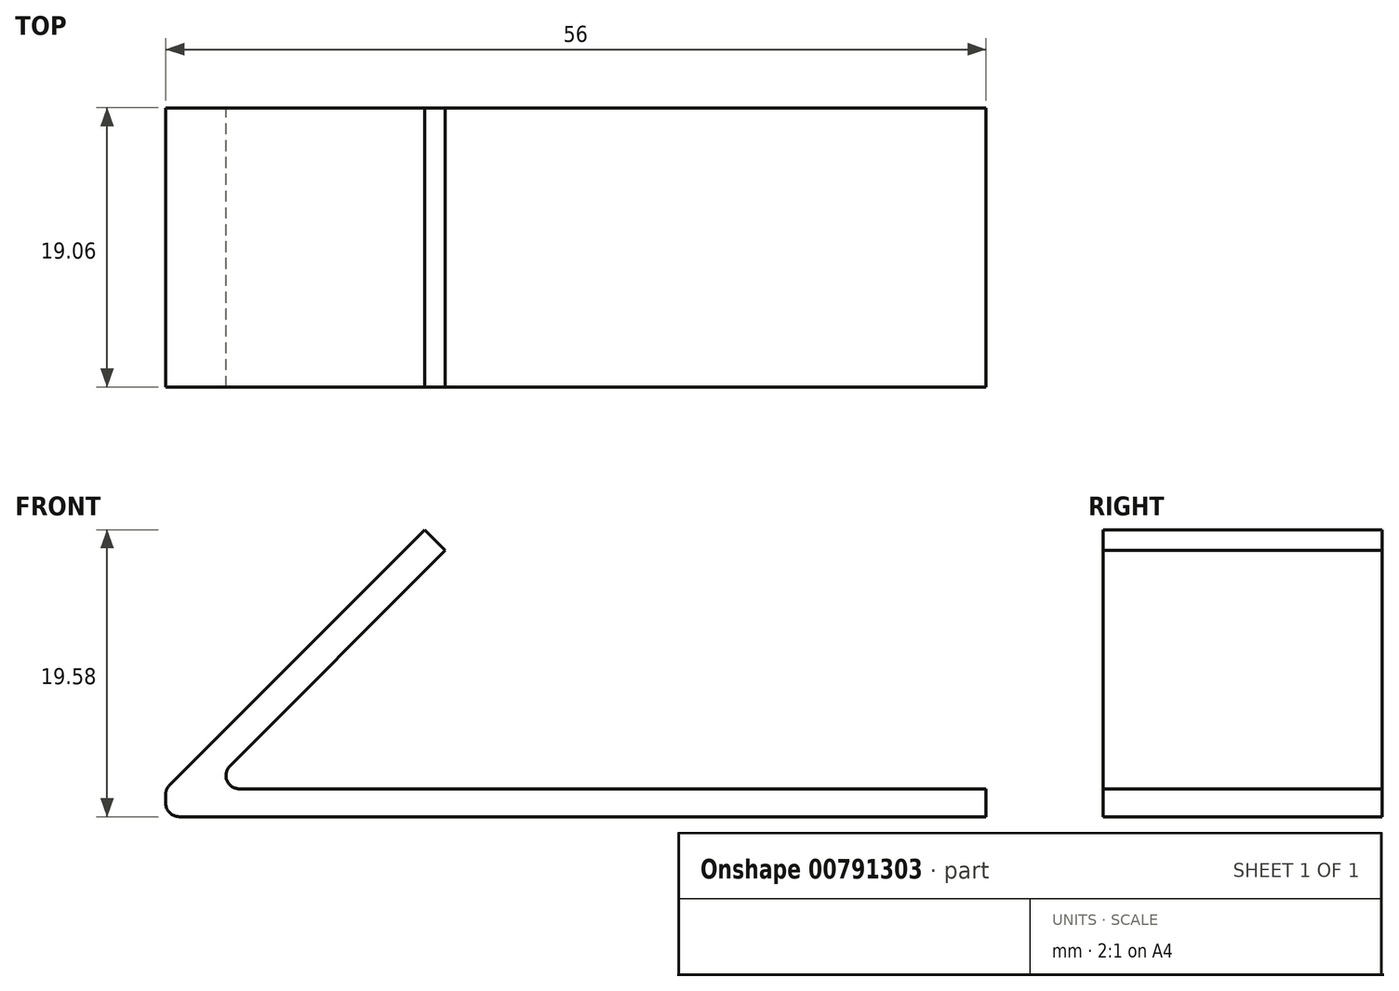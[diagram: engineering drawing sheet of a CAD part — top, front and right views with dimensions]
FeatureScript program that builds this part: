
annotation { "Feature Type Name" : "Feature", "Feature Type Description" : "" }
export const myFeature = defineFeature(function(context is Context, id is Id, definition is map)
    precondition{}
    {
        {
            var Q0;
            Q0=qCreatedBy(makeId("Front.planeOp"),FACE);
            var sketch = newSketch(context, id + "F0", { "sketchPlane" : qUnion([Q0])});
            skLineSegment(sketch, "E0.bottom", {"start": v(28, -0.95) * mm, "end": v(-27.1, -0.95) * mm});
            skLineSegment(sketch, "E0.top", {"start": v(28, 0.95) * mm, "end": v(-22.99, 0.95) * mm});
            skLineSegment(sketch, "E0.left", {"start": v(28, -0.95) * mm, "end": v(28, 0.95) * mm});
            skLineSegment(sketch, "E0.right", {"start": v(-28, -0.04) * mm, "end": v(-28, 0.57) * mm});
            skPoint(sketch, "E0.middle", {"position": v(0, 0) * mm});
            skLineSegment(sketch, "E1", {"start": v(-27.73, 1.22) * mm, "end": v(-10.32, 18.63) * mm});
            skLineSegment(sketch, "E2", {"start": v(-10.32, 18.63) * mm, "end": v(-8.91, 17.22) * mm});
            skLineSegment(sketch, "E3", {"start": v(-8.91, 17.22) * mm, "end": v(-23.63, 2.5) * mm});
            skPoint(sketch, "E4.visualSharp", {"position": v(-28, -0.95) * mm});
            skArc(sketch, "E4.filletArc", {"start": v(-28, -0.04) * mm, "mid": v(-27.73, -0.68) * mm, "end": v(-27.1, -0.95) * mm});
            skPoint(sketch, "E5.visualSharp", {"position": v(-28, 0.95) * mm});
            skArc(sketch, "E5.filletArc", {"start": v(-27.73, 1.22) * mm, "mid": v(-27.93, 0.92) * mm, "end": v(-28, 0.57) * mm});
            skArc(sketch, "E6.filletArc", {"start": v(-23.63, 2.5) * mm, "mid": v(-23.83, 1.5) * mm, "end": v(-22.99, 0.95) * mm});
            skSolve(sketch);
        }
        {
            var Q0;
            Q0 = qSketchRegion(id + "F0", true);
            extrude(context, id + "F1", {"entities" : qUnion([Q0]), "endBound" : BoundingType.SYMMETRIC, "depth" : 19.05 * mm, "offsetDistance" : 25 * mm});
        }
    });
